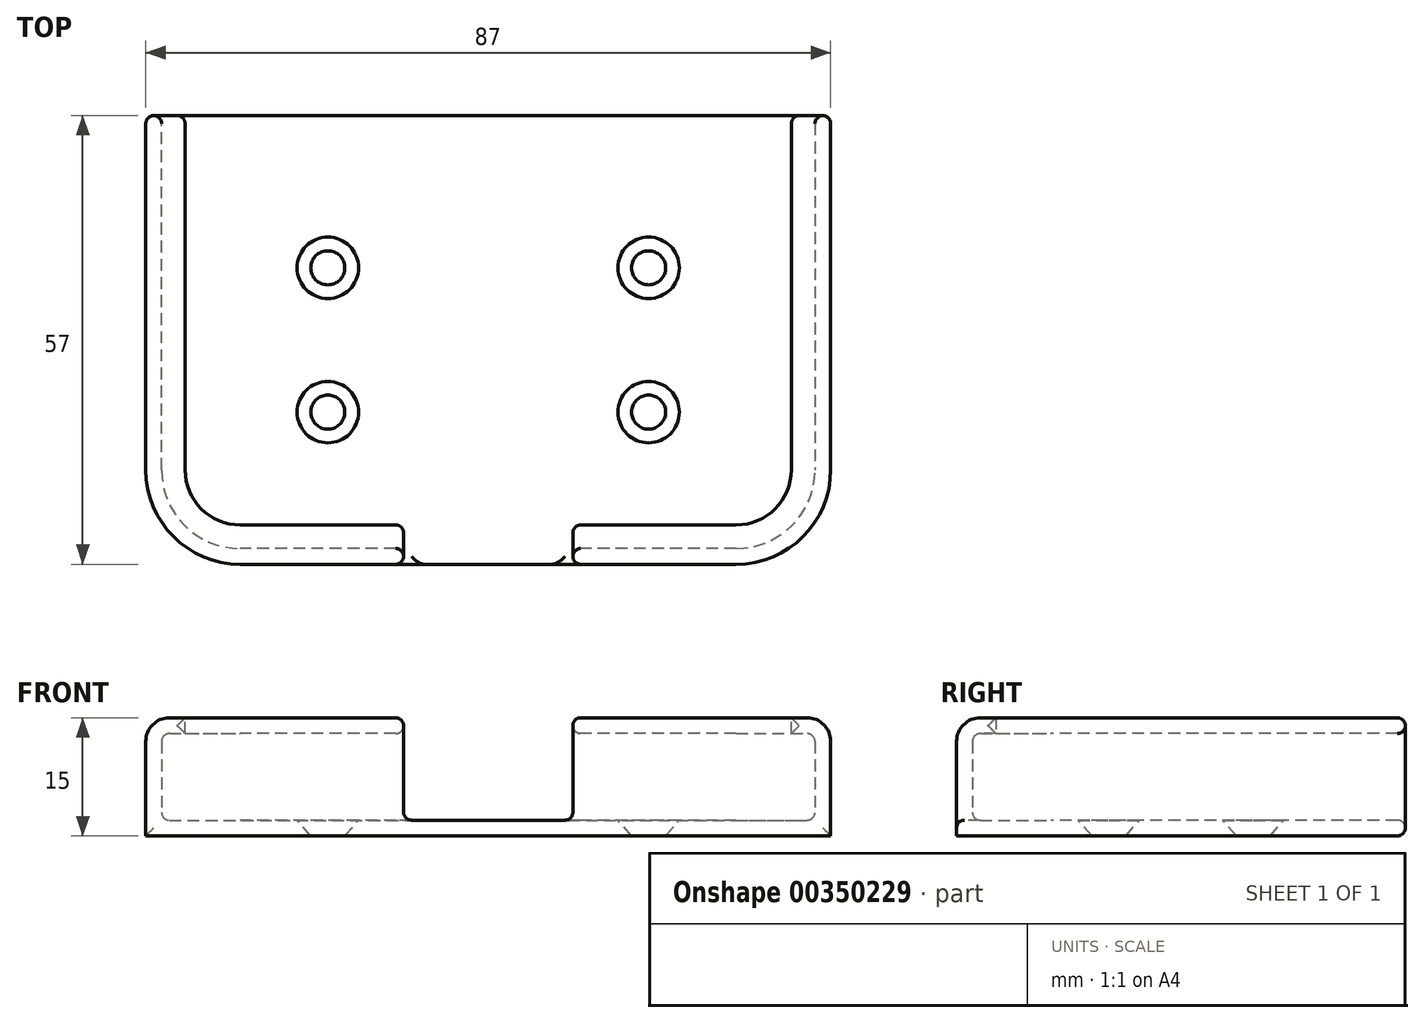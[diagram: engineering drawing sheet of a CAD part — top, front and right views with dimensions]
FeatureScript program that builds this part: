
annotation { "Feature Type Name" : "Feature", "Feature Type Description" : "" }
export const myFeature = defineFeature(function(context is Context, id is Id, definition is map)
    precondition{}
    {
        {
            assignVariable(context, id + "F0", {"name" : "PhoneThickness", "anyValue" : 9.5 * mm});
        }
        {
            assignVariable(context, id + "F1", {"name" : "EdgeRadius", "anyValue" : 1 * mm});
        }
        {
            assignVariable(context, id + "F2", {"name" : "Slop", "anyValue" : 1.5 * mm});
        }
        {
            assignVariable(context, id + "F3", {"name" : "WallThickness", "anyValue" : 2 * mm});
        }
        {
            var Q0;
            Q0=qCreatedBy(makeId("Top.planeOp"),FACE);
            var sketch = newSketch(context, id + "F4", { "sketchPlane" : qUnion([Q0])});
            skLineSegment(sketch, "E0.bottom", {"start": v(31.5, -28.5) * mm, "end": v(-31.5, -28.5) * mm});
            skLineSegment(sketch, "E0.top", {"start": v(43.5, 28.5) * mm, "end": v(-43.5, 28.5) * mm});
            skLineSegment(sketch, "E0.left", {"start": v(43.5, -16.5) * mm, "end": v(43.5, 28.5) * mm});
            skLineSegment(sketch, "E0.right", {"start": v(-43.5, -16.5) * mm, "end": v(-43.5, 28.5) * mm});
            skPoint(sketch, "E0.middle", {"position": v(0, 0) * mm});
            skPoint(sketch, "E1.visualSharp", {"position": v(-43.5, -28.5) * mm});
            skArc(sketch, "E1.filletArc", {"start": v(-43.5, -16.5) * mm, "mid": v(-39.99, -24.99) * mm, "end": v(-31.5, -28.5) * mm});
            skPoint(sketch, "E2.visualSharp", {"position": v(43.5, -28.5) * mm});
            skArc(sketch, "E2.filletArc", {"start": v(31.5, -28.5) * mm, "mid": v(39.99, -24.99) * mm, "end": v(43.5, -16.5) * mm});
            skSolve(sketch);
        }
        {
            var Q0;
            Q0 = qSketchRegion(id + "F4", true);
            extrude(context, id + "F5", {"entities" : qUnion([Q0]), "depth" : getVariable(context, 'PhoneThickness') + getVariable(context, 'Slop') + 2 * getVariable(context, 'WallThickness')});
        }
        {
            var Q0;
            Q0=makeQuery(id+"F5.opExtrude","CAP_EDGE",EDGE,{"disambiguationData":[OSD([sQuery(id+"F4.wireOp",EDGE,"E0.right")])],"isStart":false});
            var Q1;
            Q1=makeQuery(id+"F5.opExtrude","CAP_EDGE",EDGE,{"disambiguationData":[OSD([sQuery(id+"F4.wireOp",EDGE,"E1.filletArc")])],"isStart":false});
            var Q2;
            Q2=makeQuery(id+"F5.opExtrude","CAP_EDGE",EDGE,{"disambiguationData":[OSD([sQuery(id+"F4.wireOp",EDGE,"E0.bottom")])],"isStart":false});
            var Q3;
            Q3=makeQuery(id+"F5.opExtrude","CAP_EDGE",EDGE,{"disambiguationData":[OSD([sQuery(id+"F4.wireOp",EDGE,"E2.filletArc")])],"isStart":false});
            var Q4;
            Q4=makeQuery(id+"F5.opExtrude","CAP_EDGE",EDGE,{"disambiguationData":[OSD([sQuery(id+"F4.wireOp",EDGE,"E0.left")])],"isStart":false});
            fillet(context, id + "F6", {"entities" : qUnion([Q0, Q1, Q2, Q3, Q4]), "radius" : getVariable(context, 'EdgeRadius') + getVariable(context, 'WallThickness'), "tangentPropagation" : true, "allowEdgeOverflow" : false});
        }
        {
            var Q0;
            Q0=qCreatedBy(makeId("Top.planeOp"),FACE);
            cPlane(context, id + "F7", {"entities" : qUnion([Q0]), "cplaneType" : CPlaneType.OFFSET, "offset" : getVariable(context, 'WallThickness'), "width" : 152.4 * mm, "height" : 152.4 * mm});
        }
        {
            var Q0;
            Q0=qCreatedBy(id+"F7.planeOp",FACE);
            var sketch = newSketch(context, id + "F8", { "sketchPlane" : qUnion([Q0])});
            skArc(sketch, "E3.1", {"start": v(41.5, -16.5) * mm, "mid": v(38.57, -23.57) * mm, "end": v(31.5, -26.5) * mm});
            skLineSegment(sketch, "E3.2", {"start": v(31.5, -26.5) * mm, "end": v(-31.5, -26.5) * mm});
            skLineSegment(sketch, "E3.3", {"start": v(41.5, 26) * mm, "end": v(41.5, -16.5) * mm});
            skArc(sketch, "E3.4", {"start": v(-31.5, -26.5) * mm, "mid": v(-38.57, -23.57) * mm, "end": v(-41.5, -16.5) * mm});
            skLineSegment(sketch, "E3.5", {"start": v(-41.5, -16.5) * mm, "end": v(-41.5, 26) * mm});
            skLineSegment(sketch, "E4", {"start": v(-41.5, 28.5) * mm, "end": v(41.5, 28.5) * mm});
            skLineSegment(sketch, "E5", {"start": v(-41.5, 26) * mm, "end": v(-41.5, 28.5) * mm});
            skLineSegment(sketch, "E6", {"start": v(41.5, 26) * mm, "end": v(41.5, 28.5) * mm});
            skSolve(sketch);
        }
        {
            var Q0;
            Q0 = qSketchRegion(id + "F8", true);
            extrude(context, id + "F9", {"entities" : qUnion([Q0]), "operationType" : NewBodyOperationType.REMOVE, "depth" : getVariable(context, 'PhoneThickness') + getVariable(context, 'Slop')});
        }
        {
            var Q0;
            Q0=makeQuery(id+"F5.opExtrude","CAP_FACE",FACE,{"disambiguationData":[OSD([sQuery(id+"F4.wireOp",EDGE,"E0.bottom"),sQuery(id+"F4.wireOp",EDGE,"E0.top"),sQuery(id+"F4.wireOp",EDGE,"E0.left"),sQuery(id+"F4.wireOp",EDGE,"E0.right"),sQuery(id+"F4.wireOp",EDGE,"E1.filletArc"),sQuery(id+"F4.wireOp",EDGE,"E2.filletArc")])],"isStart":false});
            var sketch = newSketch(context, id + "F10", { "sketchPlane" : qUnion([Q0])});
            skLineSegment(sketch, "E7.0", {"start": v(38.5, -16.5) * mm, "end": v(38.5, 28.5) * mm});
            skLineSegment(sketch, "E7.1", {"start": v(-38.5, 28.5) * mm, "end": v(-38.5, -16.5) * mm});
            skArc(sketch, "E7.2", {"start": v(-38.5, -16.5) * mm, "mid": v(-36.45, -21.45) * mm, "end": v(-31.5, -23.5) * mm});
            skLineSegment(sketch, "E7.3", {"start": v(-31.5, -23.5) * mm, "end": v(31.5, -23.5) * mm});
            skArc(sketch, "E7.4", {"start": v(31.5, -23.5) * mm, "mid": v(36.45, -21.45) * mm, "end": v(38.5, -16.5) * mm});
            skLineSegment(sketch, "E8", {"start": v(-38.5, 28.5) * mm, "end": v(38.5, 28.5) * mm});
            skSolve(sketch);
        }
        {
            var Q0;
            Q0 = qSketchRegion(id + "F10", true);
            var Q1;
            Q1=makeQuery(id+"F9.boolean.opBoolean","COPY",FACE,{"derivedFrom":makeQuery(id+"F9.opExtrude","CAP_FACE",FACE,{"disambiguationData":[OSD([sQuery(id+"F8.wireOp",EDGE,"E3.1"),sQuery(id+"F8.wireOp",EDGE,"E3.2"),sQuery(id+"F8.wireOp",EDGE,"E3.3"),sQuery(id+"F8.wireOp",EDGE,"E3.4"),sQuery(id+"F8.wireOp",EDGE,"E3.5"),sQuery(id+"F8.wireOp",EDGE,"pnmsfDv3-1YCb-Ilsc-K5dF-sm3uTeLLsZwX"),sQuery(id+"F8.wireOp",EDGE,"yUR6LOMR-OIDv-ugbz-Swj3-6VsGYU3cq8um"),sQuery(id+"F8.wireOp",EDGE,"E4")])],"isStart":false})});
            extrude(context, id + "F11", {"entities" : qUnion([Q0]), "operationType" : NewBodyOperationType.REMOVE, "endBound" : BoundingType.UP_TO_SURFACE, "oppositeDirection" : true, "endBoundEntityFace" : qUnion([Q1]), "depth" : 25.4 * mm});
        }
        {
            var Q0;
            Q0=makeQuery(id+"F9.boolean.opBoolean","COPY",EDGE,{"derivedFrom":makeQuery(id+"F9.opExtrude","CAP_EDGE",EDGE,{"disambiguationData":[OSD([sQuery(id+"F8.wireOp",EDGE,"E3.5"),sQuery(id+"F8.wireOp",EDGE,"pnmsfDv3-1YCb-Ilsc-K5dF-sm3uTeLLsZwX")])],"isStart":false})});
            var Q1;
            Q1=makeQuery(id+"F9.boolean.opBoolean","COPY",EDGE,{"derivedFrom":makeQuery(id+"F9.opExtrude","CAP_EDGE",EDGE,{"disambiguationData":[OSD([sQuery(id+"F8.wireOp",EDGE,"E3.5"),sQuery(id+"F8.wireOp",EDGE,"pnmsfDv3-1YCb-Ilsc-K5dF-sm3uTeLLsZwX")])],"isStart":true})});
            var Q2;
            Q2=makeQuery(id+"F11.boolean.opBoolean","COPY",EDGE,{"derivedFrom":makeQuery(id+"F11.opExtrude","CAP_EDGE",EDGE,{"disambiguationData":[OSD([sQuery(id+"F10.wireOp",EDGE,"8728e2a3-5c89-44cb-a238-8fd21401300b.4")])],"isStart":true})});
            var Q3;
            Q3=makeQuery(id+"F11.boolean.opBoolean","COPY",EDGE,{"derivedFrom":makeQuery(id+"F11.opExtrude","TWEAK_EDGE",EDGE,{"derivedFrom":[makeQuery(id+"F9.boolean.opBoolean","COPY",FACE,{"derivedFrom":makeQuery(id+"F9.opExtrude","CAP_FACE",FACE,{"disambiguationData":[OSD([sQuery(id+"F8.wireOp",EDGE,"E3.1"),sQuery(id+"F8.wireOp",EDGE,"E3.2"),sQuery(id+"F8.wireOp",EDGE,"E3.3"),sQuery(id+"F8.wireOp",EDGE,"E3.4"),sQuery(id+"F8.wireOp",EDGE,"E3.5"),sQuery(id+"F8.wireOp",EDGE,"pnmsfDv3-1YCb-Ilsc-K5dF-sm3uTeLLsZwX"),sQuery(id+"F8.wireOp",EDGE,"yUR6LOMR-OIDv-ugbz-Swj3-6VsGYU3cq8um"),sQuery(id+"F8.wireOp",EDGE,"E4")])],"isStart":false})}),makeQuery(id+"F10.imprint","IMPRINT",EDGE,{"derivedFrom":sQuery(id+"F10.wireOp",EDGE,"AE57aw2j-U7KV-o0Zo-wsLR-zVzTeOUV87Z4")})]})});
            var Q4;
            Q4=makeQuery(id+"F11.boolean.opBoolean","COPY",EDGE,{"derivedFrom":makeQuery(id+"F11.opExtrude","TWEAK_EDGE",EDGE,{"derivedFrom":[makeQuery(id+"F9.boolean.opBoolean","COPY",FACE,{"derivedFrom":makeQuery(id+"F9.opExtrude","CAP_FACE",FACE,{"disambiguationData":[OSD([sQuery(id+"F8.wireOp",EDGE,"E3.1"),sQuery(id+"F8.wireOp",EDGE,"E3.2"),sQuery(id+"F8.wireOp",EDGE,"E3.3"),sQuery(id+"F8.wireOp",EDGE,"E3.4"),sQuery(id+"F8.wireOp",EDGE,"E3.5"),sQuery(id+"F8.wireOp",EDGE,"pnmsfDv3-1YCb-Ilsc-K5dF-sm3uTeLLsZwX"),sQuery(id+"F8.wireOp",EDGE,"yUR6LOMR-OIDv-ugbz-Swj3-6VsGYU3cq8um"),sQuery(id+"F8.wireOp",EDGE,"E4")])],"isStart":false})}),makeQuery(id+"F10.imprint","IMPRINT",EDGE,{"derivedFrom":sQuery(id+"F10.wireOp",EDGE,"E7.1")})]})});
            var Q5;
            Q5=makeQuery(id+"F11.boolean.opBoolean","COPY",EDGE,{"derivedFrom":makeQuery(id+"F11.opExtrude","CAP_EDGE",EDGE,{"disambiguationData":[OSD([sQuery(id+"F10.wireOp",EDGE,"E7.1")])],"isStart":true})});
            fillet(context, id + "F12", {"entities" : qUnion([Q0, Q1, Q2, Q3, Q4, Q5]), "radius" : getVariable(context, 'EdgeRadius'), "tangentPropagation" : true, "allowEdgeOverflow" : false});
        }
        {
            var Q0;
            Q0=makeQuery(id+"F9.boolean.opBoolean","COPY",FACE,{"derivedFrom":makeQuery(id+"F9.opExtrude","CAP_FACE",FACE,{"disambiguationData":[OSD([sQuery(id+"F8.wireOp",EDGE,"E3.1"),sQuery(id+"F8.wireOp",EDGE,"E3.2"),sQuery(id+"F8.wireOp",EDGE,"E3.3"),sQuery(id+"F8.wireOp",EDGE,"E3.4"),sQuery(id+"F8.wireOp",EDGE,"E3.5"),sQuery(id+"F8.wireOp",EDGE,"pnmsfDv3-1YCb-Ilsc-K5dF-sm3uTeLLsZwX"),sQuery(id+"F8.wireOp",EDGE,"yUR6LOMR-OIDv-ugbz-Swj3-6VsGYU3cq8um"),sQuery(id+"F8.wireOp",EDGE,"E4")])],"isStart":true})});
            var sketch = newSketch(context, id + "F13", { "sketchPlane" : qUnion([Q0])});
            skLineSegment(sketch, "E9.bottom", {"start": v(20.38, 9.17) * mm, "end": v(-20.38, 9.17) * mm});
            skLineSegment(sketch, "E9.top", {"start": v(20.37, -9.17) * mm, "end": v(-20.38, -9.17) * mm});
            skLineSegment(sketch, "E9.left", {"start": v(20.37, 9.17) * mm, "end": v(20.37, -9.17) * mm});
            skLineSegment(sketch, "E9.right", {"start": v(-20.38, 9.17) * mm, "end": v(-20.38, -9.17) * mm});
            skPoint(sketch, "E9.middle", {"position": v(0, 0) * mm});
            skLineSegment(sketch, "E10", {"start": v(0, 28.5) * mm, "end": v(0, -29.08) * mm});
            skPoint(sketch, "E10.endSnap0", {"position": v(0, -25.5) * mm});
            skSolve(sketch);
        }
        {
            var Q0;
            Q0=sQuery(id+"F13.wireOp",VERTEX,"E9.bottom.end");
            var Q1;
            Q1=sQuery(id+"F13.wireOp",VERTEX,"E9.left.end");
            var Q2;
            Q2=sQuery(id+"F13.wireOp",VERTEX,"E9.right.end");
            var Q3;
            Q3=sQuery(id+"F13.wireOp",VERTEX,"E9.left.start");
            var Q4;
            Q4=makeQuery(id+"F5.opExtrude","SWEPT_BODY",BODY,{"disambiguationData":[OSD([sQuery(id+"F4.wireOp",EDGE,"E0.bottom"),sQuery(id+"F4.wireOp",EDGE,"E0.top"),sQuery(id+"F4.wireOp",EDGE,"E0.left"),sQuery(id+"F4.wireOp",EDGE,"E0.right"),sQuery(id+"F4.wireOp",EDGE,"E1.filletArc"),sQuery(id+"F4.wireOp",EDGE,"E2.filletArc")])]});
            hole(context, id + "F14", {"style" : HoleStyle.C_SINK, "endStyle" : HoleEndStyle.THROUGH, "standardTappedOrClearance" : lookupTablePath({ "standard" : "ANSI", "fit" : "Normal (ASME)", "size" : "#6", "type" : "Clearance" }), "standardBlindInLast" : lookupTablePath({ "fit" : "Free", "standard" : "ANSI", "size" : "#6", "type" : "Clearance" }), "holeDiameter" : 3.8 * mm, "cSinkDiameter" : 7.8 * mm, "cSinkAngle" : 82 * degree, "isTappedThrough" : true, "tappedDepth" : 12.7 * mm, "tapClearance" : 3, "locations" : qUnion([Q0, Q1, Q2, Q3]), "scope" : qUnion([Q4])});
        }
        {
            var Q0;
            Q0=qCreatedBy(makeId("Front.planeOp"),FACE);
            var sketch = newSketch(context, id + "F15", { "sketchPlane" : qUnion([Q0])});
            skLineSegment(sketch, "E11.bottom", {"start": v(-10.75, 15) * mm, "end": v(10.75, 15) * mm});
            skLineSegment(sketch, "E11.top", {"start": v(-10.75, 2) * mm, "end": v(10.75, 2) * mm});
            skLineSegment(sketch, "E11.left", {"start": v(-10.75, 2) * mm, "end": v(-10.75, 15) * mm});
            skLineSegment(sketch, "E11.right", {"start": v(10.75, 2) * mm, "end": v(10.75, 15) * mm});
            skLineSegment(sketch, "E12", {"start": v(0, 15) * mm, "end": v(0, 0) * mm});
            skSolve(sketch);
        }
        {
            var Q0;
            Q0 = qSketchRegion(id + "F15", true);
            extrude(context, id + "F16", {"entities" : qUnion([Q0]), "operationType" : NewBodyOperationType.REMOVE, "endBound" : BoundingType.THROUGH_ALL, "depth" : 25.4 * mm});
        }
        {
            var Q0;
            Q0=makeQuery(id+"F16.boolean.opBoolean","COPY",FACE,{"derivedFrom":makeQuery(id+"F16.opExtrude","SWEPT_FACE",FACE,{"disambiguationData":[OSD([sQuery(id+"F15.wireOp",EDGE,"E11.right")])]})});
            var Q1;
            Q1=makeQuery(id+"F16.boolean.opBoolean","COPY",FACE,{"derivedFrom":makeQuery(id+"F16.opExtrude","SWEPT_FACE",FACE,{"disambiguationData":[OSD([sQuery(id+"F15.wireOp",EDGE,"E11.left")])]})});
            var Q2;
            Q2=makeQuery(id+"F5.opExtrude","SWEPT_FACE",FACE,{"disambiguationData":[OSD([sQuery(id+"F4.wireOp",EDGE,"E0.top")])]});
            fillet(context, id + "F17", {"entities" : qUnion([Q0, Q1, Q2]), "radius" : 1 * mm, "tangentPropagation" : true, "allowEdgeOverflow" : false});
        }
    });
